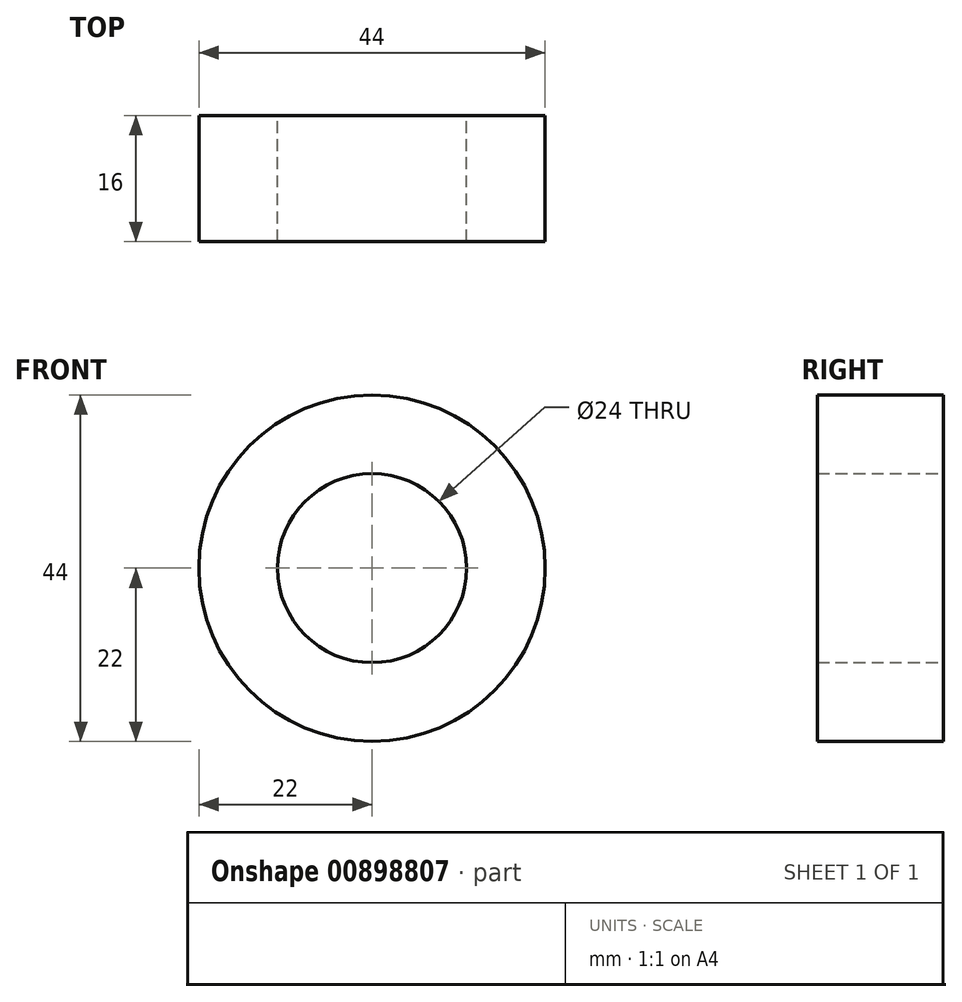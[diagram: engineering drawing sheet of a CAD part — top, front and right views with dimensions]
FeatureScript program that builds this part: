
annotation { "Feature Type Name" : "Feature", "Feature Type Description" : "" }
export const myFeature = defineFeature(function(context is Context, id is Id, definition is map)
    precondition{}
    {
        {
            var Q0;
            Q0=qCreatedBy(makeId("Front.planeOp"),FACE);
            var sketch = newSketch(context, id + "F0", { "sketchPlane" : qUnion([Q0])});
            skCircle(sketch, "E0", {"center": v(0, 0) * mm, "radius": 22 * mm});
            skCircle(sketch, "E1", {"center": v(0, 0) * mm, "radius": 12 * mm});
            skSolve(sketch);
        }
        {
            var Q0;
            Q0 = qSketchRegion(id + "F0", true);
            extrude(context, id + "F1", {"entities" : qUnion([Q0]), "depth" : 16 * mm, "offsetDistance" : 25 * mm});
        }
    });
